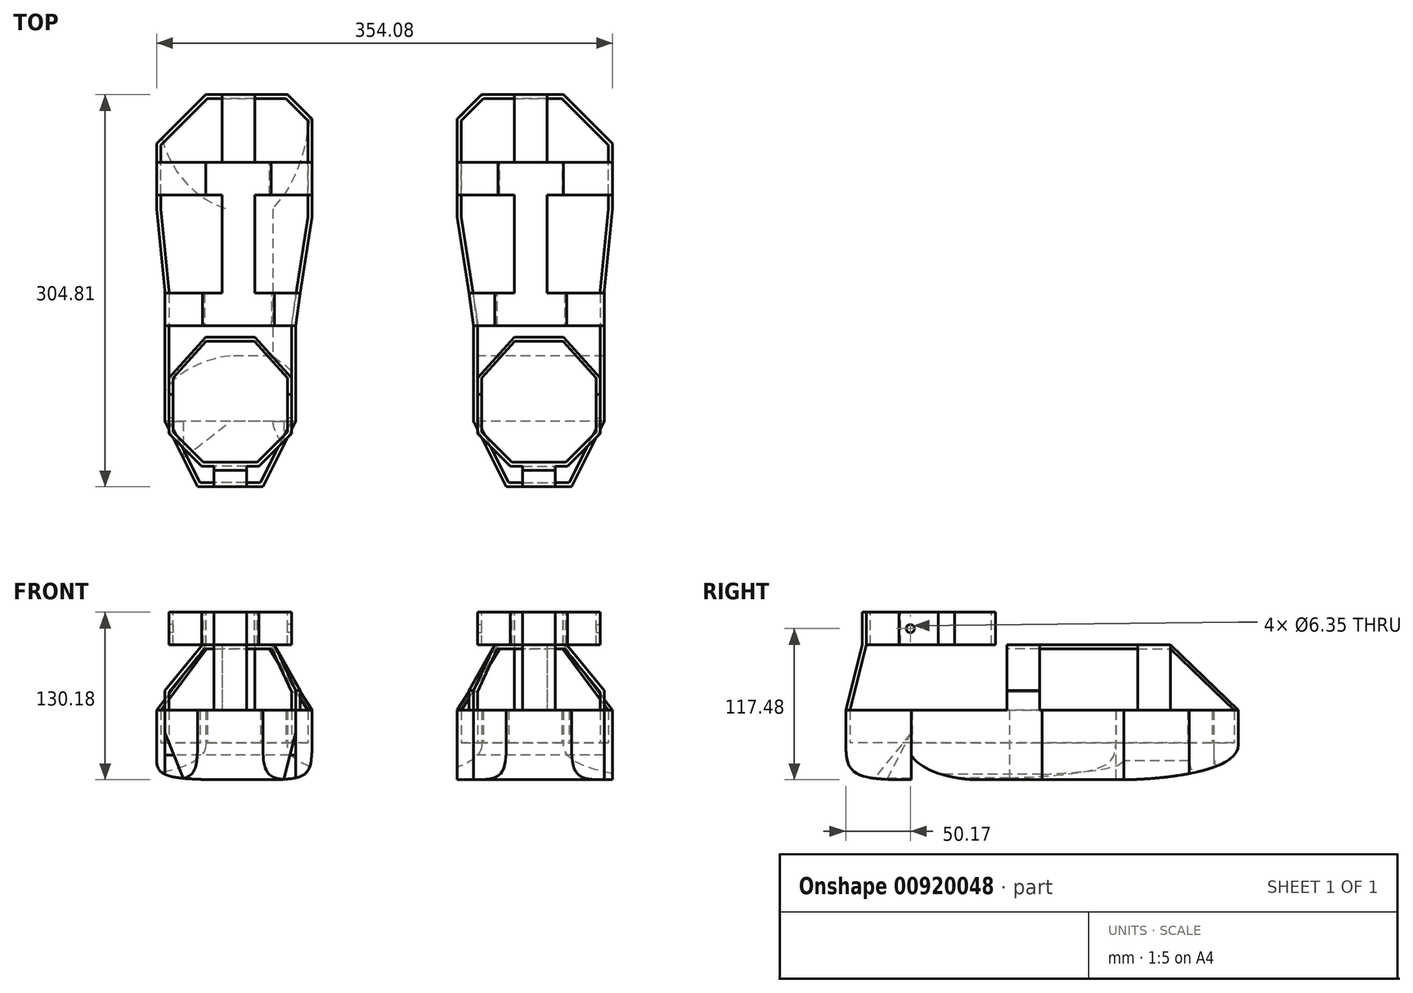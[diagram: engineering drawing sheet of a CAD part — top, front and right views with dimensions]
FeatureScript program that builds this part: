
annotation { "Feature Type Name" : "Feature", "Feature Type Description" : "" }
export const myFeature = defineFeature(function(context is Context, id is Id, definition is map)
    precondition{}
    {
        {
            var Q0;
            Q0=qCreatedBy(makeId("Top.planeOp"),FACE);
            var sketch = newSketch(context, id + "F0", { "sketchPlane" : qUnion([Q0])});
            skLineSegment(sketch, "E0", {"start": v(0, 0) * mm, "end": v(0, -30.48) * mm});
            skLineSegment(sketch, "E1", {"start": v(0, -30.48) * mm, "end": v(25.4, -55.88) * mm});
            skLineSegment(sketch, "E2", {"start": v(25.4, -55.88) * mm, "end": v(69.85, -55.88) * mm});
            skLineSegment(sketch, "E3", {"start": v(69.85, -55.88) * mm, "end": v(95.25, -30.48) * mm});
            skLineSegment(sketch, "E4", {"start": v(95.25, -30.48) * mm, "end": v(95.25, 0) * mm});
            skLineSegment(sketch, "E5.0", {"start": v(92.08, -29.16) * mm, "end": v(92.08, 0) * mm});
            skLineSegment(sketch, "E5.1", {"start": v(3.17, 0) * mm, "end": v(3.18, -29.16) * mm});
            skLineSegment(sketch, "E5.2", {"start": v(3.18, -29.16) * mm, "end": v(26.72, -52.7) * mm});
            skLineSegment(sketch, "E5.3", {"start": v(26.72, -52.7) * mm, "end": v(68.53, -52.7) * mm});
            skLineSegment(sketch, "E5.4", {"start": v(68.53, -52.7) * mm, "end": v(92.08, -29.16) * mm});
            skLineSegment(sketch, "E6", {"start": v(0, 0) * mm, "end": v(3.17, 0) * mm});
            skLineSegment(sketch, "E7", {"start": v(92.08, 0) * mm, "end": v(95.25, 0) * mm});
            skSolve(sketch);
        }
        {
            var Q0;
            Q0=makeQuery(id+"F0.imprint","IMPRINT",FACE,{"disambiguationData":[TD([[makeQuery(id+"F0.imprint","IMPRINT",EDGE,{"derivedFrom":sQuery(id+"F0.wireOp",EDGE,"E0")}),1.0]])]});
            extrude(context, id + "F1", {"entities" : qUnion([Q0]), "oppositeDirection" : true, "depth" : 25.4 * mm, "offsetDistance" : 25.4 * mm});
        }
        {
            var Q0;
            Q0=qCreatedBy(makeId("Right.planeOp"),FACE);
            var sketch = newSketch(context, id + "F2", { "sketchPlane" : qUnion([Q0])});
            skLineSegment(sketch, "E8.0", {"start": v(-55.88, -25.4) * mm, "end": v(-55.88, 0) * mm});
            skLineSegment(sketch, "E9", {"start": v(-55.88, 0) * mm, "end": v(-59.06, 0) * mm});
            skLineSegment(sketch, "E10", {"start": v(-59.06, 0) * mm, "end": v(-59.06, -25.4) * mm});
            skLineSegment(sketch, "E11", {"start": v(-55.88, -25.4) * mm, "end": v(-68.58, -76.2) * mm});
            skLineSegment(sketch, "E12", {"start": v(-68.58, -76.2) * mm, "end": v(-68.58, -101.6) * mm});
            skLineSegment(sketch, "E13", {"start": v(-68.58, -101.6) * mm, "end": v(-71.75, -101.6) * mm});
            skLineSegment(sketch, "E14", {"start": v(-71.75, -101.6) * mm, "end": v(-71.75, -76.2) * mm});
            skLineSegment(sketch, "E15", {"start": v(-71.75, -76.2) * mm, "end": v(-59.06, -25.4) * mm});
            skSolve(sketch);
        }
        {
            var Q0;
            Q0=qCreatedBy(makeId("Right.planeOp"),FACE);
            cPlane(context, id + "F3", {"entities" : qUnion([Q0]), "cplaneType" : CPlaneType.OFFSET, "offset" : 47.62 * mm, "width" : 152.4 * mm, "height" : 152.4 * mm});
        }
        {
            var Q0;
            Q0=qCreatedBy(id+"F3.planeOp",FACE);
            var sketch = newSketch(context, id + "F4", { "sketchPlane" : qUnion([Q0])});
            skLineSegment(sketch, "E16.0", {"start": v(-55.88, -25.4) * mm, "end": v(-55.88, 0) * mm});
            skLineSegment(sketch, "E17.0", {"start": v(-55.88, 0) * mm, "end": v(-59.06, 0) * mm});
            skLineSegment(sketch, "E18.0", {"start": v(-59.06, 0) * mm, "end": v(-59.06, -25.4) * mm});
            skLineSegment(sketch, "E19.0", {"start": v(-55.88, -25.4) * mm, "end": v(-68.58, -76.2) * mm});
            skLineSegment(sketch, "E20.0", {"start": v(-71.75, -76.2) * mm, "end": v(-59.06, -25.4) * mm});
            skLineSegment(sketch, "E21.0", {"start": v(-68.58, -76.2) * mm, "end": v(-68.58, -101.6) * mm});
            skLineSegment(sketch, "E22.0", {"start": v(-71.75, -101.6) * mm, "end": v(-71.75, -76.2) * mm});
            skLineSegment(sketch, "E23.0", {"start": v(-68.58, -101.6) * mm, "end": v(-71.75, -101.6) * mm});
            skSolve(sketch);
        }
        {
            var Q0;
            Q0=makeQuery(id+"F4.imprint","IMPRINT",FACE,{"disambiguationData":[TD([[makeQuery(id+"F4.imprint","IMPRINT",EDGE,{"derivedFrom":sQuery(id+"F4.wireOp",EDGE,"E16.0")}),1.0]])]});
            extrude(context, id + "F5", {"entities" : qUnion([Q0]), "operationType" : NewBodyOperationType.ADD, "depth" : 12.7 * mm, "offsetDistance" : 25.4 * mm});
        }
        {
            var Q0;
            Q0=makeQuery(id+"F5.opExtrude","CAP_FACE",FACE,{"disambiguationData":[OSD([sQuery(id+"F4.wireOp",EDGE,"E16.0"),sQuery(id+"F4.wireOp",EDGE,"E17.0"),sQuery(id+"F4.wireOp",EDGE,"E18.0"),sQuery(id+"F4.wireOp",EDGE,"E19.0"),sQuery(id+"F4.wireOp",EDGE,"E20.0"),sQuery(id+"F4.wireOp",EDGE,"E21.0"),sQuery(id+"F4.wireOp",EDGE,"E22.0"),sQuery(id+"F4.wireOp",EDGE,"E23.0")])],"isStart":true});
            extrude(context, id + "F6", {"entities" : qUnion([Q0]), "operationType" : NewBodyOperationType.ADD, "depth" : 12.7 * mm, "offsetDistance" : 25.4 * mm});
        }
        {
            var Q0;
            {var subQ0=sQuery(id+"F4.wireOp",EDGE,"E23.0");Q0=makeQuery(id+"F6.boolean.opBoolean","MERGE",FACE,{"derivedFrom":[makeQuery(id+"F5.opExtrude","SWEPT_FACE",FACE,{"disambiguationData":[OSD([subQ0])]}),makeQuery(id+"F6.opExtrude","SWEPT_FACE",FACE,{"disambiguationData":[OSD([subQ0])]})]});}
            var sketch = newSketch(context, id + "F7", { "sketchPlane" : qUnion([Q0])});
            skLineSegment(sketch, "E24", {"start": v(22.23, 71.76) * mm, "end": v(73.03, 71.76) * mm});
            skPoint(sketch, "E25.0", {"position": v(47.63, 68.58) * mm});
            skPoint(sketch, "E26", {"position": v(47.63, 71.76) * mm});
            skLineSegment(sketch, "E27", {"start": v(22.23, 71.76) * mm, "end": v(-3.18, 20.96) * mm});
            skLineSegment(sketch, "E28", {"start": v(98.43, 20.96) * mm, "end": v(73.03, 71.76) * mm});
            skLineSegment(sketch, "E29", {"start": v(-3.18, 20.96) * mm, "end": v(-3.17, -80.65) * mm});
            skLineSegment(sketch, "E30", {"start": v(-3.17, -80.64) * mm, "end": v(-9.52, -144.14) * mm});
            skLineSegment(sketch, "E31", {"start": v(-9.52, -144.14) * mm, "end": v(-9.52, -194.94) * mm});
            skLineSegment(sketch, "E32", {"start": v(-9.53, -194.94) * mm, "end": v(28.58, -233.05) * mm});
            skLineSegment(sketch, "E33", {"start": v(28.58, -233.05) * mm, "end": v(92.08, -233.05) * mm});
            skLineSegment(sketch, "E34", {"start": v(92.08, -233.05) * mm, "end": v(111.13, -214) * mm});
            skLineSegment(sketch, "E35", {"start": v(111.13, -214) * mm, "end": v(111.13, -137.8) * mm});
            skLineSegment(sketch, "E36", {"start": v(111.13, -137.8) * mm, "end": v(98.43, -55.24) * mm});
            skLineSegment(sketch, "E37", {"start": v(98.43, -55.24) * mm, "end": v(98.43, 20.96) * mm});
            skLineSegment(sketch, "E38.0", {"start": v(-6.35, -193.63) * mm, "end": v(29.9, -229.87) * mm});
            skLineSegment(sketch, "E38.1", {"start": v(95.25, -55.49) * mm, "end": v(95.25, 20.2) * mm});
            skLineSegment(sketch, "E38.2", {"start": v(107.95, -138.04) * mm, "end": v(95.25, -55.49) * mm});
            skLineSegment(sketch, "E38.3", {"start": v(107.95, -212.68) * mm, "end": v(107.95, -138.04) * mm});
            skLineSegment(sketch, "E38.4", {"start": v(90.76, -229.87) * mm, "end": v(107.95, -212.68) * mm});
            skLineSegment(sketch, "E38.5", {"start": v(95.25, 20.2) * mm, "end": v(71.06, 68.58) * mm});
            skLineSegment(sketch, "E38.6", {"start": v(29.9, -229.87) * mm, "end": v(90.76, -229.87) * mm});
            skLineSegment(sketch, "E38.7", {"start": v(24.19, 68.58) * mm, "end": v(71.06, 68.58) * mm});
            skLineSegment(sketch, "E38.8", {"start": v(24.19, 68.58) * mm, "end": v(0, 20.2) * mm});
            skLineSegment(sketch, "E38.9", {"start": v(0, 20.2) * mm, "end": v(0, -80.8) * mm});
            skLineSegment(sketch, "E38.10", {"start": v(0, -80.8) * mm, "end": v(-6.35, -144.3) * mm});
            skLineSegment(sketch, "E38.11", {"start": v(-6.35, -144.3) * mm, "end": v(-6.35, -193.63) * mm});
            skSolve(sketch);
        }
        {
            var Q0;
            {var subQ6=sQuery(id+"F7.wireOp",EDGE,"E27");Q0=makeQuery(id+"F7.imprint","IMPRINT",FACE,{"disambiguationData":[TD([[makeQuery(id+"F7.imprint","IMPRINT",EDGE,{"derivedFrom":subQ6}),1.0]])]});}
            extrude(context, id + "F8", {"entities" : qUnion([Q0]), "operationType" : NewBodyOperationType.ADD, "oppositeDirection" : true, "depth" : 25.4 * mm, "offsetDistance" : 25.4 * mm});
        }
        {
            var Q0;
            {var subQ0=sQuery(id+"F4.wireOp",EDGE,"E17.0");Q0=makeQuery(id+"F6.boolean.opBoolean","MERGE",FACE,{"derivedFrom":[makeQuery(id+"F5.boolean.opBoolean","MERGE",FACE,{"derivedFrom":[makeQuery(id+"F1.opExtrude","CAP_FACE",FACE,{"disambiguationData":[OSD([sQuery(id+"F0.wireOp",EDGE,"E0"),sQuery(id+"F0.wireOp",EDGE,"E1"),sQuery(id+"F0.wireOp",EDGE,"E2"),sQuery(id+"F0.wireOp",EDGE,"E3"),sQuery(id+"F0.wireOp",EDGE,"E4"),sQuery(id+"F0.wireOp",EDGE,"E5.0"),sQuery(id+"F0.wireOp",EDGE,"E5.1"),sQuery(id+"F0.wireOp",EDGE,"E5.2"),sQuery(id+"F0.wireOp",EDGE,"E5.3"),sQuery(id+"F0.wireOp",EDGE,"E5.4"),sQuery(id+"F0.wireOp",EDGE,"E6"),sQuery(id+"F0.wireOp",EDGE,"E7")])],"isStart":true}),makeQuery(id+"F5.opExtrude","SWEPT_FACE",FACE,{"disambiguationData":[OSD([subQ0])]})]}),makeQuery(id+"F6.opExtrude","SWEPT_FACE",FACE,{"disambiguationData":[OSD([subQ0])]})]});}
            var sketch = newSketch(context, id + "F9", { "sketchPlane" : qUnion([Q0])});
            skLineSegment(sketch, "E39", {"start": v(28.9, 41.28) * mm, "end": v(66.36, 41.28) * mm});
            skLineSegment(sketch, "E40", {"start": v(66.68, 44.45) * mm, "end": v(28.58, 44.45) * mm});
            skLineSegment(sketch, "E41", {"start": v(3.17, 0) * mm, "end": v(0, 0) * mm});
            skLineSegment(sketch, "E42", {"start": v(0, 0) * mm, "end": v(0, 12.7) * mm});
            skLineSegment(sketch, "E43", {"start": v(3.17, 12.7) * mm, "end": v(3.17, 0) * mm});
            skLineSegment(sketch, "E44", {"start": v(92.08, 0) * mm, "end": v(92.08, 12.7) * mm});
            skLineSegment(sketch, "E45", {"start": v(95.25, 12.7) * mm, "end": v(95.25, 0) * mm});
            skLineSegment(sketch, "E46", {"start": v(95.25, 0) * mm, "end": v(92.08, 0) * mm});
            skLineSegment(sketch, "E47", {"start": v(66.36, 41.28) * mm, "end": v(92.08, 12.7) * mm});
            skLineSegment(sketch, "E48", {"start": v(95.25, 12.7) * mm, "end": v(66.68, 44.45) * mm});
            skLineSegment(sketch, "E49", {"start": v(28.9, 41.28) * mm, "end": v(3.17, 12.7) * mm});
            skLineSegment(sketch, "E50", {"start": v(28.58, 44.45) * mm, "end": v(0, 12.7) * mm});
            skSolve(sketch);
        }
        {
            var Q0;
            Q0=makeQuery(id+"F9.imprint","IMPRINT",FACE,{"disambiguationData":[TD([[makeQuery(id+"F9.imprint","IMPRINT",EDGE,{"derivedFrom":sQuery(id+"F9.wireOp",EDGE,"E39")}),1.0]])]});
            extrude(context, id + "F10", {"entities" : qUnion([Q0]), "oppositeDirection" : true, "depth" : 25.4 * mm, "offsetDistance" : 25.4 * mm});
        }
        {
            var Q0;
            {var subQ0=sQuery(id+"F4.wireOp",EDGE,"E23.0");Q0=makeQuery(id+"F8.boolean.opBoolean","MERGE",FACE,{"derivedFrom":[makeQuery(id+"F6.boolean.opBoolean","MERGE",FACE,{"derivedFrom":[makeQuery(id+"F5.opExtrude","SWEPT_FACE",FACE,{"disambiguationData":[OSD([subQ0])]}),makeQuery(id+"F6.opExtrude","SWEPT_FACE",FACE,{"disambiguationData":[OSD([subQ0])]})]}),makeQuery(id+"F8.opExtrude","CAP_FACE",FACE,{"disambiguationData":[OSD([subQ0,sQuery(id+"F7.wireOp",EDGE,"E24"),sQuery(id+"F7.wireOp",EDGE,"E27"),sQuery(id+"F7.wireOp",EDGE,"E28"),sQuery(id+"F7.wireOp",EDGE,"E29"),sQuery(id+"F7.wireOp",EDGE,"E30"),sQuery(id+"F7.wireOp",EDGE,"E31"),sQuery(id+"F7.wireOp",EDGE,"E32"),sQuery(id+"F7.wireOp",EDGE,"E33"),sQuery(id+"F7.wireOp",EDGE,"E34"),sQuery(id+"F7.wireOp",EDGE,"E35"),sQuery(id+"F7.wireOp",EDGE,"E36"),sQuery(id+"F7.wireOp",EDGE,"E37"),sQuery(id+"F7.wireOp",EDGE,"E38.0"),sQuery(id+"F7.wireOp",EDGE,"E38.1"),sQuery(id+"F7.wireOp",EDGE,"E38.2"),sQuery(id+"F7.wireOp",EDGE,"E38.3"),sQuery(id+"F7.wireOp",EDGE,"E38.4"),sQuery(id+"F7.wireOp",EDGE,"E38.5"),sQuery(id+"F7.wireOp",EDGE,"E38.6"),sQuery(id+"F7.wireOp",EDGE,"E38.7"),sQuery(id+"F7.wireOp",EDGE,"E38.8"),sQuery(id+"F7.wireOp",EDGE,"E38.9"),sQuery(id+"F7.wireOp",EDGE,"E38.10"),sQuery(id+"F7.wireOp",EDGE,"E38.11")])],"isStart":true})]});}
            var sketch = newSketch(context, id + "F11", { "sketchPlane" : qUnion([Q0])});
            skLineSegment(sketch, "E51.0", {"start": v(-3.18, 20.96) * mm, "end": v(-3.17, -80.64) * mm});
            skLineSegment(sketch, "E52.0", {"start": v(22.23, 71.76) * mm, "end": v(-3.18, 20.95) * mm});
            skLineSegment(sketch, "E53.0", {"start": v(73.03, 71.76) * mm, "end": v(22.23, 71.76) * mm});
            skLineSegment(sketch, "E54.0", {"start": v(98.43, 20.96) * mm, "end": v(73.03, 71.76) * mm});
            skLineSegment(sketch, "E55.0", {"start": v(98.43, -55.24) * mm, "end": v(98.43, 20.96) * mm});
            skLineSegment(sketch, "E56.0", {"start": v(111.13, -137.8) * mm, "end": v(98.43, -55.25) * mm});
            skLineSegment(sketch, "E57.0", {"start": v(111.13, -214) * mm, "end": v(111.13, -137.8) * mm});
            skLineSegment(sketch, "E58.0", {"start": v(92.08, -233.05) * mm, "end": v(111.13, -214) * mm});
            skLineSegment(sketch, "E59.0", {"start": v(28.58, -233.05) * mm, "end": v(92.08, -233.05) * mm});
            skLineSegment(sketch, "E60.0", {"start": v(-9.53, -194.94) * mm, "end": v(28.58, -233.05) * mm});
            skLineSegment(sketch, "E61.0", {"start": v(-9.52, -144.14) * mm, "end": v(-9.52, -194.94) * mm});
            skLineSegment(sketch, "E62.0", {"start": v(-3.17, -80.64) * mm, "end": v(-9.52, -144.14) * mm});
            skSolve(sketch);
        }
        {
            var Q0;
            Q0=makeQuery(id+"F11.imprint","IMPRINT",FACE,{"disambiguationData":[TD([[makeQuery(id+"F11.imprint","IMPRINT",EDGE,{"derivedFrom":makeQuery(id+"F8.opExtrude","CAP_EDGE",EDGE,{"disambiguationData":[OSD([sQuery(id+"F7.wireOp",EDGE,"E38.0")])],"isStart":true})}),1.0]])]});
            var Q1;
            Q1=makeQuery(id+"F11.imprint","IMPRINT",FACE,{"disambiguationData":[TD([[makeQuery(id+"F11.imprint","IMPRINT",EDGE,{"derivedFrom":sQuery(id+"F11.wireOp",EDGE,"E51.0")}),1.0]])]});
            extrude(context, id + "F12", {"entities" : qUnion([Q0, Q1]), "operationType" : NewBodyOperationType.ADD, "depth" : 3.17 * mm, "offsetDistance" : 25.4 * mm});
        }
        {
            var Q0;
            Q0=makeQuery(id+"F12.opExtrude","CAP_FACE",FACE,{"disambiguationData":[OSD([sQuery(id+"F11.wireOp",EDGE,"E51.0"),sQuery(id+"F11.wireOp",EDGE,"E52.0"),sQuery(id+"F11.wireOp",EDGE,"E53.0"),sQuery(id+"F11.wireOp",EDGE,"E54.0"),sQuery(id+"F11.wireOp",EDGE,"E55.0"),sQuery(id+"F11.wireOp",EDGE,"E56.0"),sQuery(id+"F11.wireOp",EDGE,"E57.0"),sQuery(id+"F11.wireOp",EDGE,"E58.0"),sQuery(id+"F11.wireOp",EDGE,"E59.0"),sQuery(id+"F11.wireOp",EDGE,"E60.0"),sQuery(id+"F11.wireOp",EDGE,"E61.0"),sQuery(id+"F11.wireOp",EDGE,"E62.0")])],"isStart":false});
            extrude(context, id + "F13", {"entities" : qUnion([Q0]), "operationType" : NewBodyOperationType.ADD, "depth" : 25.4 * mm, "offsetDistance" : 25.4 * mm});
        }
        {
            var Q0;
            Q0=qCreatedBy(id+"F3.planeOp",FACE);
            var sketch = newSketch(context, id + "F14", { "sketchPlane" : qUnion([Q0])});
            skLineSegment(sketch, "E63.bottom", {"start": v(59.7, -25.4) * mm, "end": v(180.34, -25.4) * mm});
            skLineSegment(sketch, "E63.top", {"start": v(59.7, -28.57) * mm, "end": v(180.46, -28.57) * mm});
            skLineSegment(sketch, "E63.left", {"start": v(59.7, -25.4) * mm, "end": v(59.7, -28.57) * mm});
            skPoint(sketch, "E64.0", {"position": v(233.05, -76.2) * mm});
            skPoint(sketch, "E65.0", {"position": v(229.87, -76.2) * mm});
            skLineSegment(sketch, "E66", {"start": v(180.34, -25.4) * mm, "end": v(233.05, -76.2) * mm});
            skLineSegment(sketch, "E67", {"start": v(180.46, -28.57) * mm, "end": v(229.87, -76.2) * mm});
            skLineSegment(sketch, "E68", {"start": v(233.05, -76.2) * mm, "end": v(229.87, -76.2) * mm});
            skSolve(sketch);
        }
        {
            var Q0;
            Q0=makeQuery(id+"F14.imprint","IMPRINT",FACE,{"disambiguationData":[TD([[makeQuery(id+"F14.imprint","IMPRINT",EDGE,{"derivedFrom":sQuery(id+"F14.wireOp",EDGE,"E63.bottom")}),-1.0]])]});
            extrude(context, id + "F15", {"entities" : qUnion([Q0]), "depth" : 19.05 * mm, "offsetDistance" : 25.4 * mm, "hasSecondDirection" : true, "secondDirectionOppositeDirection" : true, "secondDirectionDepth" : 6.35 * mm});
        }
        {
            var Q0;
            Q0=qCreatedBy(makeId("Front.planeOp"),FACE);
            var Q1;
            Q1=makeQuery(id+"F15.opExtrude","CAP_VERTEX",VERTEX,{"disambiguationData":[OSD([sQuery(id+"F14.wireOp",EDGE,"E63.bottom"),sQuery(id+"F14.wireOp",EDGE,"E66")])],"isStart":true});
            cPlane(context, id + "F16", {"entities" : qUnion([Q0, Q1]), "cplaneType" : CPlaneType.PLANE_POINT, "offset" : 25.4 * mm, "width" : 152.4 * mm, "height" : 152.4 * mm});
        }
        {
            var Q0;
            Q0=qCreatedBy(id+"F16.planeOp",FACE);
            var sketch = newSketch(context, id + "F17", { "sketchPlane" : qUnion([Q0])});
            skPoint(sketch, "E69.0", {"position": v(41.28, -25.4) * mm});
            skPoint(sketch, "E70.0", {"position": v(-9.53, -76.2) * mm});
            skPoint(sketch, "E71.0", {"position": v(41.28, -28.57) * mm});
            skPoint(sketch, "E72.0", {"position": v(-6.35, -76.2) * mm});
            skLineSegment(sketch, "E73", {"start": v(41.28, -25.4) * mm, "end": v(28.58, -25.4) * mm});
            skLineSegment(sketch, "E74", {"start": v(28.58, -25.4) * mm, "end": v(-9.53, -76.2) * mm});
            skLineSegment(sketch, "E75", {"start": v(-6.35, -76.2) * mm, "end": v(-9.53, -76.2) * mm});
            skLineSegment(sketch, "E76", {"start": v(-6.35, -76.2) * mm, "end": v(29.37, -28.57) * mm});
            skLineSegment(sketch, "E77", {"start": v(29.37, -28.57) * mm, "end": v(41.28, -28.57) * mm});
            skLineSegment(sketch, "E78", {"start": v(41.28, -25.4) * mm, "end": v(41.28, -28.57) * mm});
            skSolve(sketch);
        }
        {
            var Q0;
            Q0=makeQuery(id+"F17.imprint","IMPRINT",FACE,{"disambiguationData":[TD([[makeQuery(id+"F17.imprint","IMPRINT",EDGE,{"derivedFrom":sQuery(id+"F17.wireOp",EDGE,"E73")}),1.0]])]});
            extrude(context, id + "F18", {"entities" : qUnion([Q0]), "operationType" : NewBodyOperationType.ADD, "depth" : 25.4 * mm, "offsetDistance" : 25.4 * mm});
        }
        {
            var Q0;
            Q0=qCreatedBy(id+"F16.planeOp",FACE);
            var sketch = newSketch(context, id + "F19", { "sketchPlane" : qUnion([Q0])});
            skPoint(sketch, "E79.0", {"position": v(66.68, -25.4) * mm});
            skPoint(sketch, "E80.0", {"position": v(66.68, -28.57) * mm});
            skPoint(sketch, "E81.0", {"position": v(111.13, -76.2) * mm});
            skPoint(sketch, "E82.0", {"position": v(107.95, -76.2) * mm});
            skLineSegment(sketch, "E83", {"start": v(66.68, -25.4) * mm, "end": v(79.38, -25.4) * mm});
            skLineSegment(sketch, "E84", {"start": v(79.38, -25.4) * mm, "end": v(111.13, -76.2) * mm});
            skLineSegment(sketch, "E85", {"start": v(111.13, -76.2) * mm, "end": v(107.95, -76.2) * mm});
            skLineSegment(sketch, "E86", {"start": v(107.95, -76.2) * mm, "end": v(78.18, -28.57) * mm});
            skLineSegment(sketch, "E87", {"start": v(78.18, -28.57) * mm, "end": v(66.68, -28.57) * mm});
            skLineSegment(sketch, "E88", {"start": v(66.68, -28.57) * mm, "end": v(66.68, -25.4) * mm});
            skSolve(sketch);
        }
        {
            var Q0;
            Q0=makeQuery(id+"F19.imprint","IMPRINT",FACE,{"disambiguationData":[TD([[makeQuery(id+"F19.imprint","IMPRINT",EDGE,{"derivedFrom":sQuery(id+"F19.wireOp",EDGE,"E83")}),-1.0]])]});
            extrude(context, id + "F20", {"entities" : qUnion([Q0]), "operationType" : NewBodyOperationType.ADD, "depth" : 25.4 * mm, "offsetDistance" : 25.4 * mm});
        }
        {
            var Q0;
            Q0=makeQuery(id+"F15.opExtrude","SWEPT_FACE",FACE,{"disambiguationData":[OSD([sQuery(id+"F14.wireOp",EDGE,"E63.left")])]});
            var sketch = newSketch(context, id + "F21", { "sketchPlane" : qUnion([Q0])});
            skPoint(sketch, "E89.0", {"position": v(41.28, -25.4) * mm});
            skPoint(sketch, "E90.0", {"position": v(41.28, -28.57) * mm});
            skPoint(sketch, "E91.0", {"position": v(0, -76.2) * mm});
            skPoint(sketch, "E92.0", {"position": v(-3.17, -76.2) * mm});
            skLineSegment(sketch, "E93", {"start": v(0, -76.2) * mm, "end": v(0, -62.1) * mm});
            skLineSegment(sketch, "E94", {"start": v(0, -62.1) * mm, "end": v(27.54, -28.57) * mm});
            skLineSegment(sketch, "E95", {"start": v(27.54, -28.57) * mm, "end": v(41.28, -28.57) * mm});
            skLineSegment(sketch, "E96", {"start": v(41.28, -25.4) * mm, "end": v(41.28, -28.57) * mm});
            skLineSegment(sketch, "E97", {"start": v(41.28, -25.4) * mm, "end": v(26.04, -25.4) * mm});
            skLineSegment(sketch, "E98", {"start": v(26.04, -25.4) * mm, "end": v(-3.17, -60.96) * mm});
            skLineSegment(sketch, "E99", {"start": v(-3.17, -60.96) * mm, "end": v(-3.17, -76.2) * mm});
            skLineSegment(sketch, "E100", {"start": v(-3.17, -76.2) * mm, "end": v(0, -76.2) * mm});
            skSolve(sketch);
        }
        {
            var Q0;
            Q0=makeQuery(id+"F21.imprint","IMPRINT",FACE,{"disambiguationData":[TD([[makeQuery(id+"F21.imprint","IMPRINT",EDGE,{"derivedFrom":sQuery(id+"F21.wireOp",EDGE,"E93")}),1.0]])]});
            extrude(context, id + "F22", {"entities" : qUnion([Q0]), "operationType" : NewBodyOperationType.ADD, "oppositeDirection" : true, "depth" : 19.05 * mm, "offsetDistance" : 25.4 * mm, "hasSecondDirection" : true, "secondDirectionOppositeDirection" : false, "secondDirectionDepth" : 6.35 * mm});
        }
        {
            var Q0;
            Q0=makeQuery(id+"F15.opExtrude","SWEPT_FACE",FACE,{"disambiguationData":[OSD([sQuery(id+"F14.wireOp",EDGE,"E63.left")])]});
            var Q1;
            Q1=makeQuery(id+"F22.opExtrude","CAP_FACE",FACE,{"disambiguationData":[OSD([sQuery(id+"F21.wireOp",EDGE,"E93"),sQuery(id+"F21.wireOp",EDGE,"E94"),sQuery(id+"F21.wireOp",EDGE,"E95"),sQuery(id+"F21.wireOp",EDGE,"E96"),sQuery(id+"F21.wireOp",EDGE,"E97"),sQuery(id+"F21.wireOp",EDGE,"E98"),sQuery(id+"F21.wireOp",EDGE,"E99"),sQuery(id+"F21.wireOp",EDGE,"E100")])],"isStart":true});
            extrude(context, id + "F23", {"entities" : qUnion([Q0]), "operationType" : NewBodyOperationType.ADD, "endBound" : BoundingType.UP_TO_SURFACE, "depth" : 25.4 * mm, "endBoundEntityFace" : qUnion([Q1]), "offsetDistance" : 25.4 * mm});
        }
        {
            var Q0;
            Q0=makeQuery(id+"F23.boolean.opBoolean","MERGE",FACE,{"derivedFrom":[makeQuery(id+"F22.opExtrude","CAP_FACE",FACE,{"disambiguationData":[OSD([sQuery(id+"F21.wireOp",EDGE,"E93"),sQuery(id+"F21.wireOp",EDGE,"E94"),sQuery(id+"F21.wireOp",EDGE,"E95"),sQuery(id+"F21.wireOp",EDGE,"E96"),sQuery(id+"F21.wireOp",EDGE,"E97"),sQuery(id+"F21.wireOp",EDGE,"E98"),sQuery(id+"F21.wireOp",EDGE,"E99"),sQuery(id+"F21.wireOp",EDGE,"E100")])],"isStart":true}),makeQuery(id+"F23.opExtrude","CAP_FACE",FACE,{"disambiguationData":[OSD([sQuery(id+"F14.wireOp",EDGE,"E63.left")])],"isStart":false})]});
            var sketch = newSketch(context, id + "F24", { "sketchPlane" : qUnion([Q0])});
            skPoint(sketch, "E101.0", {"position": v(66.68, -25.4) * mm});
            skPoint(sketch, "E102.0", {"position": v(66.68, -26.99) * mm});
            skPoint(sketch, "E103.0", {"position": v(66.68, -28.57) * mm});
            skPoint(sketch, "E104.0", {"position": v(98.43, -76.2) * mm});
            skPoint(sketch, "E105.0", {"position": v(95.25, -76.2) * mm});
            skLineSegment(sketch, "E106", {"start": v(98.43, -76.2) * mm, "end": v(98.43, -60.96) * mm});
            skLineSegment(sketch, "E107", {"start": v(66.68, -25.4) * mm, "end": v(66.68, -28.57) * mm});
            skLineSegment(sketch, "E108", {"start": v(95.25, -61.66) * mm, "end": v(95.25, -76.2) * mm});
            skLineSegment(sketch, "E109", {"start": v(95.25, -76.2) * mm, "end": v(98.43, -76.2) * mm});
            skLineSegment(sketch, "E110", {"start": v(66.68, -25.4) * mm, "end": v(81.92, -25.4) * mm});
            skLineSegment(sketch, "E111", {"start": v(81.92, -25.4) * mm, "end": v(98.43, -60.96) * mm});
            skLineSegment(sketch, "E112", {"start": v(95.25, -61.66) * mm, "end": v(79.89, -28.57) * mm});
            skLineSegment(sketch, "E113", {"start": v(79.89, -28.57) * mm, "end": v(66.68, -28.57) * mm});
            skSolve(sketch);
        }
        {
            var Q0;
            Q0=makeQuery(id+"F8.opExtrude","CAP_FACE",FACE,{"disambiguationData":[OSD([sQuery(id+"F4.wireOp",EDGE,"E23.0"),sQuery(id+"F7.wireOp",EDGE,"E24"),sQuery(id+"F7.wireOp",EDGE,"E27"),sQuery(id+"F7.wireOp",EDGE,"E28"),sQuery(id+"F7.wireOp",EDGE,"E29"),sQuery(id+"F7.wireOp",EDGE,"E30"),sQuery(id+"F7.wireOp",EDGE,"E31"),sQuery(id+"F7.wireOp",EDGE,"E32"),sQuery(id+"F7.wireOp",EDGE,"E33"),sQuery(id+"F7.wireOp",EDGE,"E34"),sQuery(id+"F7.wireOp",EDGE,"E35"),sQuery(id+"F7.wireOp",EDGE,"E36"),sQuery(id+"F7.wireOp",EDGE,"E37"),sQuery(id+"F7.wireOp",EDGE,"E38.0"),sQuery(id+"F7.wireOp",EDGE,"E38.1"),sQuery(id+"F7.wireOp",EDGE,"E38.2"),sQuery(id+"F7.wireOp",EDGE,"E38.3"),sQuery(id+"F7.wireOp",EDGE,"E38.4"),sQuery(id+"F7.wireOp",EDGE,"E38.5"),sQuery(id+"F7.wireOp",EDGE,"E38.6"),sQuery(id+"F7.wireOp",EDGE,"E38.7"),sQuery(id+"F7.wireOp",EDGE,"E38.8"),sQuery(id+"F7.wireOp",EDGE,"E38.9"),sQuery(id+"F7.wireOp",EDGE,"E38.10"),sQuery(id+"F7.wireOp",EDGE,"E38.11")])],"isStart":false});
            var sketch = newSketch(context, id + "F25", { "sketchPlane" : qUnion([Q0])});
            skPoint(sketch, "E114.0", {"position": v(95.25, 55.49) * mm});
            skPoint(sketch, "E115.0", {"position": v(98.43, 55.24) * mm});
            skLineSegment(sketch, "E116.0", {"start": v(101.97, 78.26) * mm, "end": v(98.43, 55.25) * mm});
            skLineSegment(sketch, "E117.0", {"start": v(98.83, 78.74) * mm, "end": v(95.25, 55.49) * mm});
            skPoint(sketch, "E118.0", {"position": v(95.25, 53.34) * mm});
            skPoint(sketch, "E119.0", {"position": v(98.43, 53.34) * mm});
            skLineSegment(sketch, "E120", {"start": v(98.43, 53.34) * mm, "end": v(95.25, 53.34) * mm});
            skLineSegment(sketch, "E121", {"start": v(95.25, 55.49) * mm, "end": v(95.25, 53.34) * mm});
            skLineSegment(sketch, "E122", {"start": v(95.25, 55.49) * mm, "end": v(98.83, 78.74) * mm});
            skLineSegment(sketch, "E123", {"start": v(101.97, 78.26) * mm, "end": v(98.43, 55.24) * mm});
            skLineSegment(sketch, "E124", {"start": v(98.43, 55.25) * mm, "end": v(98.43, 53.34) * mm});
            skPoint(sketch, "E125.orphan", {"position": v(111.13, 137.8) * mm});
            skPoint(sketch, "E126.orphan", {"position": v(107.95, 138.04) * mm});
            skLineSegment(sketch, "E127", {"start": v(98.83, 78.74) * mm, "end": v(102.04, 78.74) * mm});
            skLineSegment(sketch, "E128", {"start": v(101.97, 78.26) * mm, "end": v(102.04, 78.74) * mm});
            skSolve(sketch);
        }
        {
            var Q0;
            Q0=sQuery(id+"F25.wireOp",EDGE,"E127");
            cPoint(context, id + "F26", {"entities" : qUnion([Q0]), "parameter" : 0.5});
        }
        {
            var Q0;
            Q0=qCreatedBy(makeId("Front.planeOp"),FACE);
            var Q1;
            Q1 = qCreatedBy(id + "F26" ,VERTEX);
            cPlane(context, id + "F27", {"entities" : qUnion([Q0, Q1]), "cplaneType" : CPlaneType.PLANE_POINT, "offset" : 25.4 * mm, "width" : 152.4 * mm, "height" : 152.4 * mm});
        }
        {
            var Q0;
            Q0=qCreatedBy(id+"F27.planeOp",FACE);
            var sketch = newSketch(context, id + "F28", { "sketchPlane" : qUnion([Q0])});
            skPoint(sketch, "E129.0", {"position": v(66.68, -25.4) * mm});
            skPoint(sketch, "E130.0", {"position": v(66.68, -28.57) * mm});
            skPoint(sketch, "E131.0", {"position": v(98.83, -76.2) * mm});
            skPoint(sketch, "E132.0", {"position": v(102.04, -76.2) * mm});
            skLineSegment(sketch, "E133", {"start": v(102.04, -76.2) * mm, "end": v(102.04, -60.96) * mm});
            skLineSegment(sketch, "E134", {"start": v(102.04, -60.96) * mm, "end": v(81.92, -25.4) * mm});
            skLineSegment(sketch, "E135", {"start": v(81.92, -25.4) * mm, "end": v(66.68, -25.4) * mm});
            skLineSegment(sketch, "E136", {"start": v(66.68, -28.57) * mm, "end": v(80.06, -28.57) * mm});
            skLineSegment(sketch, "E137", {"start": v(80.06, -28.57) * mm, "end": v(98.83, -61.73) * mm});
            skLineSegment(sketch, "E138", {"start": v(98.83, -61.73) * mm, "end": v(98.83, -76.2) * mm});
            skLineSegment(sketch, "E139", {"start": v(66.68, -25.4) * mm, "end": v(66.68, -28.57) * mm});
            skLineSegment(sketch, "E140", {"start": v(102.04, -76.2) * mm, "end": v(98.83, -76.2) * mm});
            skSolve(sketch);
        }
        {
            var Q1;
            Q1=makeQuery(id+"F24.imprint","IMPRINT",FACE,{"disambiguationData":[TD([[makeQuery(id+"F24.imprint","IMPRINT",EDGE,{"derivedFrom":sQuery(id+"F24.wireOp",EDGE,"E106")}),1.0]])]});
            var Q2;
            Q2=makeQuery(id+"F28.imprint","IMPRINT",FACE,{"disambiguationData":[TD([[makeQuery(id+"F28.imprint","IMPRINT",EDGE,{"derivedFrom":sQuery(id+"F28.wireOp",EDGE,"E133")}),1.0]])]});
            loft(context, id + "F29", {"operationType" : NewBodyOperationType.ADD, "sheetProfilesArray" : [{ "sheetProfileEntities" : qUnion([Q1]) }, { "sheetProfileEntities" : qUnion([Q2]) }]});
        }
        {
            var Q0;
            Q0=qCreatedBy(id+"F3.planeOp",FACE);
            cPlane(context, id + "F30", {"entities" : qUnion([Q0]), "cplaneType" : CPlaneType.OFFSET, "offset" : 119.89 * mm, "width" : 152.4 * mm, "height" : 152.4 * mm});
        }
        {
            var Q0;
            Q0=qCreatedBy(makeId("Front.planeOp"),FACE);
            var sketch = newSketch(context, id + "F31", { "sketchPlane" : qUnion([Q0])});
            skPoint(sketch, "E141.0", {"position": v(0, -25.4) * mm});
            skPoint(sketch, "E142.0", {"position": v(-3.18, -76.2) * mm});
            skPoint(sketch, "E143.0", {"position": v(0, -76.2) * mm});
            skLineSegment(sketch, "E144", {"start": v(0, 0) * mm, "end": v(0, -25.4) * mm});
            skLineSegment(sketch, "E145", {"start": v(0, -25.4) * mm, "end": v(0, -76.2) * mm});
            skLineSegment(sketch, "E146", {"start": v(0, -76.2) * mm, "end": v(-3.18, -76.2) * mm});
            skLineSegment(sketch, "E147", {"start": v(-3.18, -76.2) * mm, "end": v(-3.18, 0) * mm});
            skLineSegment(sketch, "E148", {"start": v(0, 0) * mm, "end": v(-3.18, 0) * mm});
            skSolve(sketch);
        }
        {
            var Q0;
            {var subQ0=sQuery(id+"F11.wireOp",EDGE,"E51.0");Q0=makeQuery(id+"FWAyXbKwRlu94lJ_3.boolean.opBoolean","MERGE",FACE,{"derivedFrom":[makeQuery(id+"F13.boolean.opBoolean","MERGE",FACE,{"derivedFrom":[makeQuery(id+"F12.boolean.opBoolean","MERGE",FACE,{"derivedFrom":[makeQuery(id+"F8.opExtrude","SWEPT_FACE",FACE,{"disambiguationData":[OSD([sQuery(id+"F7.wireOp",EDGE,"E29")])]}),makeQuery(id+"F12.opExtrude","SWEPT_FACE",FACE,{"disambiguationData":[OSD([subQ0])]})]}),makeQuery(id+"F13.opExtrude","SWEPT_FACE",FACE,{"disambiguationData":[OSD([subQ0])]})]}),makeQuery(id+"FWAyXbKwRlu94lJ_3.opExtrude","SWEPT_FACE",FACE,{"disambiguationData":[OSD([sQuery(id+"F31.wireOp",EDGE,"E147")])]})]});}
            var sketch = newSketch(context, id + "F32", { "sketchPlane" : qUnion([Q0])});
            skCircle(sketch, "E149", {"center": v(21.59, -12.7) * mm, "radius": 3.18 * mm});
            skSolve(sketch);
        }
        {
            var Q0;
            Q0=makeQuery(id+"F32.imprint","IMPRINT",FACE,{"disambiguationData":[TD([[makeQuery(id+"F32.imprint","IMPRINT",EDGE,{"derivedFrom":sQuery(id+"F32.wireOp",EDGE,"E149")}),1.0]])]});
            extrude(context, id + "F33", {"entities" : qUnion([Q0]), "operationType" : NewBodyOperationType.REMOVE, "endBound" : BoundingType.THROUGH_ALL, "oppositeDirection" : true, "depth" : 25.4 * mm, "offsetDistance" : 25.4 * mm});
        }
        {
            var Q0;
            Q0=makeQuery(id+"F15.opExtrude","SWEPT_BODY",BODY,{"disambiguationData":[OSD([sQuery(id+"F14.wireOp",EDGE,"E63.bottom"),sQuery(id+"F14.wireOp",EDGE,"E63.top"),sQuery(id+"F14.wireOp",EDGE,"E63.left"),sQuery(id+"F14.wireOp",EDGE,"E66"),sQuery(id+"F14.wireOp",EDGE,"E67"),sQuery(id+"F14.wireOp",EDGE,"E68")])]});
            var Q1;
            Q1=makeQuery(id+"F1.opExtrude","SWEPT_BODY",BODY,{"disambiguationData":[OSD([sQuery(id+"F0.wireOp",EDGE,"E0"),sQuery(id+"F0.wireOp",EDGE,"E1"),sQuery(id+"F0.wireOp",EDGE,"E2"),sQuery(id+"F0.wireOp",EDGE,"E3"),sQuery(id+"F0.wireOp",EDGE,"E4"),sQuery(id+"F0.wireOp",EDGE,"E5.0"),sQuery(id+"F0.wireOp",EDGE,"E5.1"),sQuery(id+"F0.wireOp",EDGE,"E5.2"),sQuery(id+"F0.wireOp",EDGE,"E5.3"),sQuery(id+"F0.wireOp",EDGE,"E5.4"),sQuery(id+"F0.wireOp",EDGE,"E6"),sQuery(id+"F0.wireOp",EDGE,"E7")])]});
            var Q2;
            Q2=makeQuery(id+"F10.opExtrude","SWEPT_BODY",BODY,{"disambiguationData":[OSD([sQuery(id+"F9.wireOp",EDGE,"E39"),sQuery(id+"F9.wireOp",EDGE,"E40"),sQuery(id+"F9.wireOp",EDGE,"E41"),sQuery(id+"F9.wireOp",EDGE,"E42"),sQuery(id+"F9.wireOp",EDGE,"E43"),sQuery(id+"F9.wireOp",EDGE,"E44"),sQuery(id+"F9.wireOp",EDGE,"E45"),sQuery(id+"F9.wireOp",EDGE,"E46"),sQuery(id+"F9.wireOp",EDGE,"E47"),sQuery(id+"F9.wireOp",EDGE,"E48"),sQuery(id+"F9.wireOp",EDGE,"E49"),sQuery(id+"F9.wireOp",EDGE,"E50")])]});
            var Q3;
            Q3=qCreatedBy(id+"F30.planeOp",FACE);
            mirror(context, id + "F34", {"entities" : qUnion([Q0, Q1, Q2]), "mirrorPlane" : qUnion([Q3])});
        }
        {
            var Q0;
            Q0=qCreatedBy(id+"F3.planeOp",FACE);
            cPlane(context, id + "F35", {"entities" : qUnion([Q0]), "cplaneType" : CPlaneType.OFFSET, "offset" : 136.65 * mm, "oppositeDirection" : true, "width" : 152.4 * mm, "height" : 152.4 * mm});
        }
        {
            var Q0;
            Q0=qCreatedBy(id+"F35.planeOp",FACE);
            var sketch = newSketch(context, id + "F36", { "sketchPlane" : qUnion([Q0])});
            skLineSegment(sketch, "E150.0", {"start": v(233.05, -103.19) * mm, "end": v(233.05, -130.17) * mm});
            skLineSegment(sketch, "E151.0", {"start": v(194.94, -130.17) * mm, "end": v(233.05, -130.17) * mm});
            skLineSegment(sketch, "E152.0", {"start": v(-71.76, -130.18) * mm, "end": v(-20.95, -130.18) * mm});
            skLineSegment(sketch, "E153.0", {"start": v(-71.76, -103.19) * mm, "end": v(-71.75, -130.17) * mm});
            skFitSpline(sketch, "E154", {"points": [v(-20.95, -130.18) * mm, v(-71.76, -103.19) * mm], "startDerivative": vector(-128.28, 0) * mm, "endDerivative": vector(0, 72.98) * mm});
            skFitSpline(sketch, "E155", {"points": [v(233.05, -103.19) * mm, v(144.15, -130.17) * mm], "startDerivative": vector(0, -65.03) * mm, "endDerivative": vector(-78.57, -0.63) * mm});
            skPoint(sketch, "E156.orphan", {"position": v(233.05, -76.2) * mm});
            skPoint(sketch, "E157.orphan", {"position": v(-71.76, -76.2) * mm});
            skLineSegment(sketch, "E158", {"start": v(194.94, -130.17) * mm, "end": v(144.15, -130.17) * mm});
            skPoint(sketch, "E159.0", {"position": v(29.85, -130.18) * mm});
            skLineSegment(sketch, "E160.0", {"start": v(-20.95, -111.13) * mm, "end": v(-20.95, -130.17) * mm});
            skFitSpline(sketch, "E161", {"points": [v(29.85, -130.18) * mm, v(-23.68, -103.91) * mm], "startDerivative": vector(-58.47, 0.98) * mm, "endDerivative": vector(-8.18, 56.14) * mm});
            skLineSegment(sketch, "E162", {"start": v(-20.95, -111.13) * mm, "end": v(-20.95, -130.18) * mm});
            skLineSegment(sketch, "E163", {"start": v(-20.95, -130.18) * mm, "end": v(29.85, -130.18) * mm});
            skPoint(sketch, "E164.orphan", {"position": v(-20.95, -76.2) * mm});
            skSolve(sketch);
        }
        {
            var Q0;
            Q0=makeQuery(id+"F36.imprint","IMPRINT",FACE,{"disambiguationData":[TD([[makeQuery(id+"F36.imprint","IMPRINT",EDGE,{"derivedFrom":sQuery(id+"F36.wireOp",EDGE,"E150.0")}),-1.0]])]});
            var Q1;
            Q1=makeQuery(id+"F36.imprint","IMPRINT",FACE,{"disambiguationData":[TD([[makeQuery(id+"F36.imprint","IMPRINT",EDGE,{"derivedFrom":sQuery(id+"F36.wireOp",EDGE,"E152.0")}),1.0]])]});
            var Q2;
            Q2=makeQuery(id+"F36.imprint","IMPRINT",FACE,{"disambiguationData":[TD([[makeQuery(id+"F36.imprint","IMPRINT",EDGE,{"derivedFrom":sQuery(id+"F36.wireOp",EDGE,"E161")}),1.0]])]});
            extrude(context, id + "F37", {"entities" : qUnion([Q0, Q1, Q2]), "operationType" : NewBodyOperationType.REMOVE, "endBound" : BoundingType.THROUGH_ALL, "depth" : 25.4 * mm, "offsetDistance" : 25.4 * mm});
        }
        {
            var Q0;
            {var subQ0=sQuery(id+"F11.wireOp",EDGE,"E53.0");var subQ1=sQuery(id+"F7.wireOp",EDGE,"E24");var subQ2=sQuery(id+"F4.wireOp",EDGE,"E23.0");var subQ3=sQuery(id+"F4.wireOp",EDGE,"E22.0");Q0=makeQuery(id+"F13.boolean.opBoolean","MERGE",FACE,{"derivedFrom":[makeQuery(id+"F12.boolean.opBoolean","MERGE",FACE,{"derivedFrom":[makeQuery(id+"F8.boolean.opBoolean","MERGE",FACE,{"derivedFrom":[makeQuery(id+"F6.boolean.opBoolean","MERGE",FACE,{"derivedFrom":[makeQuery(id+"F5.opExtrude","SWEPT_FACE",FACE,{"disambiguationData":[OSD([subQ3])]}),makeQuery(id+"F6.opExtrude","SWEPT_FACE",FACE,{"disambiguationData":[OSD([subQ3])]})]}),makeQuery(id+"F8.opExtrude","SWEPT_FACE",FACE,{"disambiguationData":[OSD([subQ1]),TDD([makeQuery(id+"F7.imprint","IMPRINT",EDGE,{"disambiguationData":[TD([[makeQuery(id+"F7.imprint","INTERSECT",VERTEX,{"derivedFrom":[makeQuery(id+"F6.opExtrude","CAP_EDGE",EDGE,{"disambiguationData":[OSD([subQ2])],"isStart":false}),subQ1]}),1.0],[makeQuery(id+"F7.imprint","INTERSECT",VERTEX,{"derivedFrom":[subQ1,sQuery(id+"F7.wireOp",EDGE,"E27")]}),-1.0]])],"derivedFrom":subQ1})])]}),makeQuery(id+"F8.opExtrude","SWEPT_FACE",FACE,{"disambiguationData":[OSD([subQ1]),TDD([makeQuery(id+"F7.imprint","IMPRINT",EDGE,{"disambiguationData":[TD([[makeQuery(id+"F7.imprint","INTERSECT",VERTEX,{"derivedFrom":[makeQuery(id+"F5.opExtrude","CAP_EDGE",EDGE,{"disambiguationData":[OSD([subQ2])],"isStart":false}),subQ1]}),-1.0],[makeQuery(id+"F7.imprint","INTERSECT",VERTEX,{"derivedFrom":[subQ1,sQuery(id+"F7.wireOp",EDGE,"E28")]}),1.0]])],"derivedFrom":subQ1})])]})]}),makeQuery(id+"F12.opExtrude","SWEPT_FACE",FACE,{"disambiguationData":[OSD([subQ0])]})]}),makeQuery(id+"F13.opExtrude","SWEPT_FACE",FACE,{"disambiguationData":[OSD([subQ0])]})]});}
            var sketch = newSketch(context, id + "F38", { "sketchPlane" : qUnion([Q0])});
            skPoint(sketch, "E165.0", {"position": v(-9.52, -103.19) * mm});
            skPoint(sketch, "E166.0", {"position": v(111.13, -103.19) * mm});
            skPoint(sketch, "E167.0", {"position": v(-9.53, -130.17) * mm});
            skPoint(sketch, "E168.0", {"position": v(111.13, -130.17) * mm});
            skFitSpline(sketch, "E169", {"points": [v(47.63, -130.18) * mm, v(-9.52, -103.19) * mm], "startDerivative": vector(-186.86, 0) * mm, "endDerivative": vector(0, 69.58) * mm});
            skFitSpline(sketch, "E170", {"points": [v(47.63, -130.18) * mm, v(111.13, -103.19) * mm], "startDerivative": vector(176.92, 0) * mm, "endDerivative": vector(0, 89.2) * mm});
            skLineSegment(sketch, "E171", {"start": v(47.63, -130.17) * mm, "end": v(111.13, -130.17) * mm});
            skLineSegment(sketch, "E172", {"start": v(111.13, -130.17) * mm, "end": v(111.13, -103.19) * mm});
            skLineSegment(sketch, "E173", {"start": v(-9.53, -130.17) * mm, "end": v(-9.52, -103.19) * mm});
            skLineSegment(sketch, "E174", {"start": v(47.63, -130.18) * mm, "end": v(-9.53, -130.17) * mm});
            skSolve(sketch);
        }
        {
            var Q0;
            {var subQ0=sQuery(id+"F38.wireOp",EDGE,"GDIvorta-bJ40-JhsW-ZxaV-srddWiT8vVEK");var subQ3=sQuery(id+"F38.wireOp",EDGE,"E173");var subQ5=makeQuery(id+"F38.imprint","INTERSECT",VERTEX,{"derivedFrom":[subQ0,subQ3]});Q0=makeQuery(id+"F38.imprint","IMPRINT",FACE,{"disambiguationData":[TD([[makeQuery(id+"F38.imprint","IMPRINT",EDGE,{"disambiguationData":[TD([[subQ5,-1.0]])],"derivedFrom":subQ3}),-1.0]])]});}
            var Q1;
            {var subQ0=sQuery(id+"F38.wireOp",EDGE,"E172");Q1=makeQuery(id+"F38.imprint","IMPRINT",FACE,{"disambiguationData":[TD([[makeQuery(id+"F38.imprint","IMPRINT",EDGE,{"derivedFrom":subQ0}),1.0]])]});}
            extrude(context, id + "F39", {"entities" : qUnion([Q0, Q1]), "operationType" : NewBodyOperationType.REMOVE, "endBound" : BoundingType.THROUGH_ALL, "oppositeDirection" : true, "depth" : 25.4 * mm, "offsetDistance" : 25.4 * mm});
        }
        {
            var Q0;
            {var subQ0=sQuery(id+"F11.wireOp",EDGE,"E53.0");var subQ1=sQuery(id+"F7.wireOp",EDGE,"E24");var subQ2=sQuery(id+"F4.wireOp",EDGE,"E23.0");var subQ3=sQuery(id+"F4.wireOp",EDGE,"E22.0");Q0=makeQuery(id+"F13.boolean.opBoolean","MERGE",FACE,{"derivedFrom":[makeQuery(id+"F12.boolean.opBoolean","MERGE",FACE,{"derivedFrom":[makeQuery(id+"F8.boolean.opBoolean","MERGE",FACE,{"derivedFrom":[makeQuery(id+"F6.boolean.opBoolean","MERGE",FACE,{"derivedFrom":[makeQuery(id+"F5.opExtrude","SWEPT_FACE",FACE,{"disambiguationData":[OSD([subQ3])]}),makeQuery(id+"F6.opExtrude","SWEPT_FACE",FACE,{"disambiguationData":[OSD([subQ3])]})]}),makeQuery(id+"F8.opExtrude","SWEPT_FACE",FACE,{"disambiguationData":[OSD([subQ1]),TDD([makeQuery(id+"F7.imprint","IMPRINT",EDGE,{"disambiguationData":[TD([[makeQuery(id+"F7.imprint","INTERSECT",VERTEX,{"derivedFrom":[makeQuery(id+"F6.opExtrude","CAP_EDGE",EDGE,{"disambiguationData":[OSD([subQ2])],"isStart":false}),subQ1]}),1.0],[makeQuery(id+"F7.imprint","INTERSECT",VERTEX,{"derivedFrom":[subQ1,sQuery(id+"F7.wireOp",EDGE,"E27")]}),-1.0]])],"derivedFrom":subQ1})])]}),makeQuery(id+"F8.opExtrude","SWEPT_FACE",FACE,{"disambiguationData":[OSD([subQ1]),TDD([makeQuery(id+"F7.imprint","IMPRINT",EDGE,{"disambiguationData":[TD([[makeQuery(id+"F7.imprint","INTERSECT",VERTEX,{"derivedFrom":[makeQuery(id+"F5.opExtrude","CAP_EDGE",EDGE,{"disambiguationData":[OSD([subQ2])],"isStart":false}),subQ1]}),-1.0],[makeQuery(id+"F7.imprint","INTERSECT",VERTEX,{"derivedFrom":[subQ1,sQuery(id+"F7.wireOp",EDGE,"E28")]}),1.0]])],"derivedFrom":subQ1})])]})]}),makeQuery(id+"F12.opExtrude","SWEPT_FACE",FACE,{"disambiguationData":[OSD([subQ0])]})]}),makeQuery(id+"F13.opExtrude","SWEPT_FACE",FACE,{"disambiguationData":[OSD([subQ0])]})]});}
            var sketch = newSketch(context, id + "F40", { "sketchPlane" : qUnion([Q0])});
            skPoint(sketch, "E175.0", {"position": v(89.12, -129.87) * mm});
            skPoint(sketch, "E176.0", {"position": v(11.12, -129.1) * mm});
            skPoint(sketch, "E177.0", {"position": v(-3.18, -93.66) * mm});
            skPoint(sketch, "E178.0", {"position": v(98.43, -93.66) * mm});
            skLineSegment(sketch, "E179", {"start": v(89.12, -129.87) * mm, "end": v(98.43, -93.66) * mm});
            skLineSegment(sketch, "E180", {"start": v(98.43, -93.66) * mm, "end": v(98.43, -129.87) * mm});
            skLineSegment(sketch, "E181", {"start": v(89.12, -129.87) * mm, "end": v(98.43, -129.87) * mm});
            skLineSegment(sketch, "E182", {"start": v(-3.18, -93.66) * mm, "end": v(11.12, -129.1) * mm});
            skLineSegment(sketch, "E183", {"start": v(11.12, -129.1) * mm, "end": v(-3.18, -129.87) * mm});
            skLineSegment(sketch, "E184", {"start": v(-3.18, -93.66) * mm, "end": v(-3.18, -129.87) * mm});
            skSolve(sketch);
        }
        {
            var Q0;
            Q0=makeQuery(id+"F40.imprint","IMPRINT",FACE,{"disambiguationData":[TD([[makeQuery(id+"F40.imprint","IMPRINT",EDGE,{"derivedFrom":sQuery(id+"F40.wireOp",EDGE,"E182")}),-1.0]])]});
            var Q1;
            Q1=makeQuery(id+"F40.imprint","IMPRINT",FACE,{"disambiguationData":[TD([[makeQuery(id+"F40.imprint","IMPRINT",EDGE,{"derivedFrom":sQuery(id+"F40.wireOp",EDGE,"E179")}),-1.0]])]});
            var Q2;
            Q2=makeQuery(id+"F37.boolean.opBoolean","COPY",FACE,{"disambiguationData":[TD([makeQuery(id+"F8.opExtrude","SWEPT_FACE",FACE,{"disambiguationData":[OSD([sQuery(id+"F7.wireOp",EDGE,"E27")])]})])],"derivedFrom":makeQuery(id+"F37.opExtrude","SWEPT_FACE",FACE,{"disambiguationData":[OSD([sQuery(id+"F36.wireOp",EDGE,"E162")])]})});
            extrude(context, id + "F41", {"entities" : qUnion([Q0, Q1]), "operationType" : NewBodyOperationType.REMOVE, "endBound" : BoundingType.UP_TO_SURFACE, "oppositeDirection" : true, "depth" : 25.4 * mm, "endBoundEntityFace" : qUnion([Q2]), "offsetDistance" : 25.4 * mm});
        }
    });
